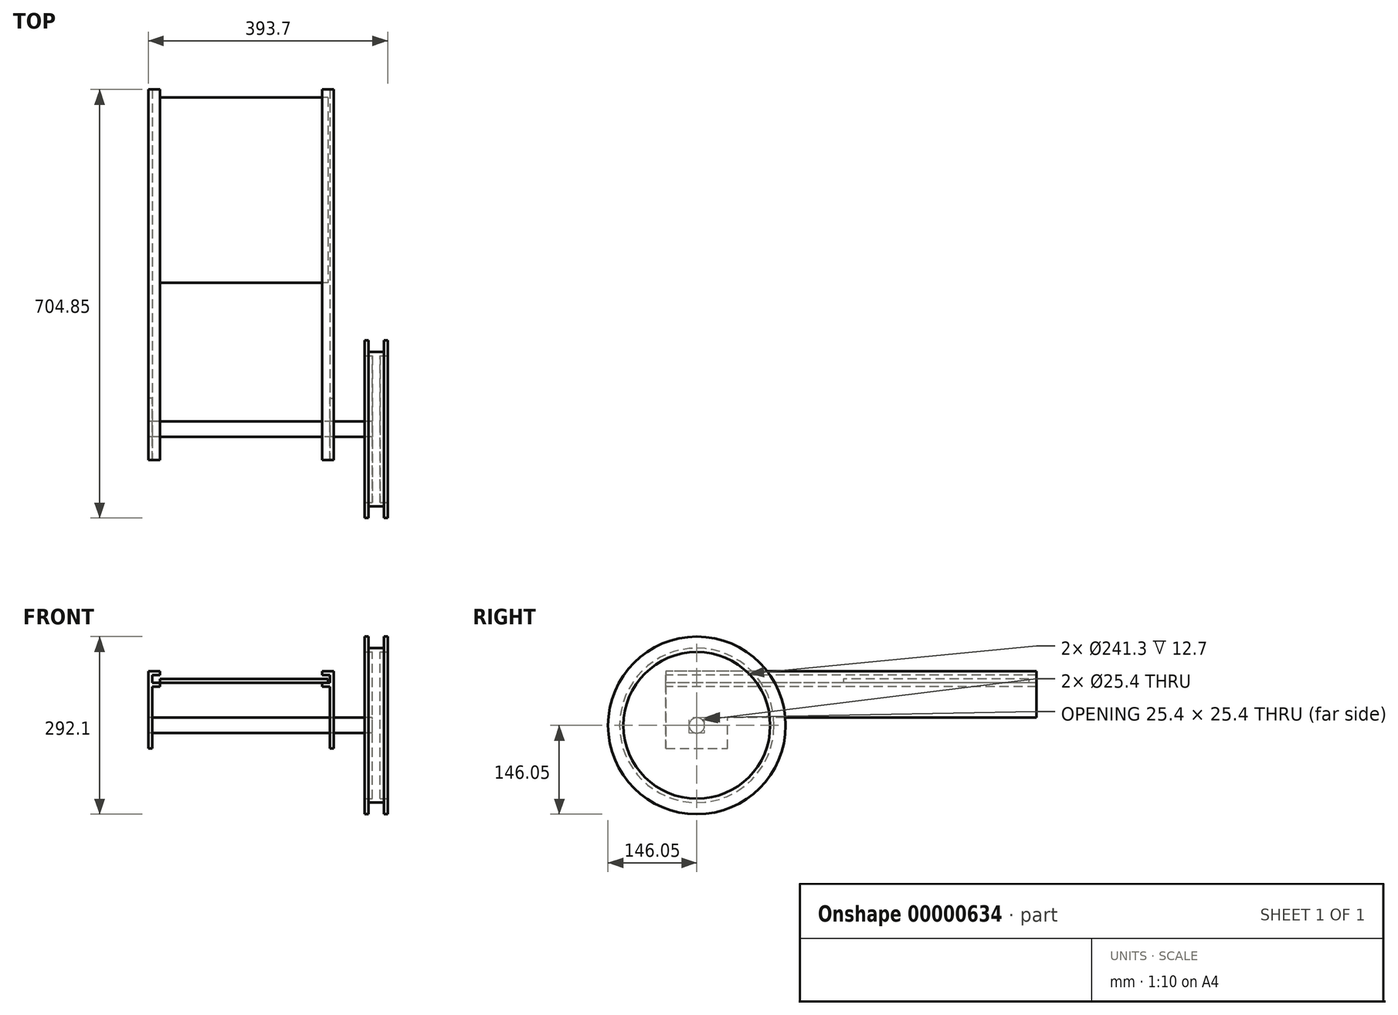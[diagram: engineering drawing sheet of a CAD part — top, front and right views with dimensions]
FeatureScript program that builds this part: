
annotation { "Feature Type Name" : "Feature", "Feature Type Description" : "" }
export const myFeature = defineFeature(function(context is Context, id is Id, definition is map)
    precondition{}
    {
        {
            var Q0;
            Q0=qCreatedBy(makeId("Front.planeOp"),FACE);
            var sketch = newSketch(context, id + "F0", { "sketchPlane" : qUnion([Q0])});
            skLineSegment(sketch, "E0", {"start": v(-152.4, 76.2) * mm, "end": v(-152.4, -50.8) * mm});
            skLineSegment(sketch, "E1", {"start": v(-152.4, -50.8) * mm, "end": v(-146.05, -50.8) * mm});
            skLineSegment(sketch, "E2", {"start": v(-146.05, 50.8) * mm, "end": v(-133.35, 50.8) * mm});
            skLineSegment(sketch, "E3", {"start": v(-133.35, 57.15) * mm, "end": v(-146.05, 57.15) * mm});
            skLineSegment(sketch, "E4", {"start": v(-146.05, 57.15) * mm, "end": v(-146.05, 69.85) * mm});
            skLineSegment(sketch, "E5", {"start": v(-146.05, 69.85) * mm, "end": v(-133.35, 69.85) * mm});
            skLineSegment(sketch, "E6", {"start": v(-133.35, 50.8) * mm, "end": v(-133.35, 57.15) * mm});
            skLineSegment(sketch, "E7", {"start": v(-133.35, 76.2) * mm, "end": v(-152.4, 76.2) * mm});
            skLineSegment(sketch, "E8", {"start": v(-146.05, -50.8) * mm, "end": v(-146.05, 50.8) * mm});
            skLineSegment(sketch, "E9", {"start": v(-146.05, 0) * mm, "end": v(-152.4, 0) * mm});
            skLineSegment(sketch, "E10", {"start": v(-133.35, 76.2) * mm, "end": v(-133.35, 69.85) * mm});
            skLineSegment(sketch, "E11", {"start": v(0, 0) * mm, "end": v(0, 73.55) * mm, "construction": true});
            skLineSegment(sketch, "E12.0.MirrorCS", {"start": v(146.05, -50.8) * mm, "end": v(146.05, 50.8) * mm});
            skLineSegment(sketch, "E12.1.MirrorCS", {"start": v(133.35, 50.8) * mm, "end": v(133.35, 57.15) * mm});
            skLineSegment(sketch, "E12.2.MirrorCS", {"start": v(146.05, 50.8) * mm, "end": v(133.35, 50.8) * mm});
            skLineSegment(sketch, "E12.3.MirrorCS", {"start": v(133.35, 76.2) * mm, "end": v(152.4, 76.2) * mm});
            skLineSegment(sketch, "E12.4.MirrorCS", {"start": v(152.4, -50.8) * mm, "end": v(146.05, -50.8) * mm});
            skLineSegment(sketch, "E12.5.MirrorCS", {"start": v(146.05, 69.85) * mm, "end": v(133.35, 69.85) * mm});
            skLineSegment(sketch, "E12.6.MirrorCS", {"start": v(146.05, 0) * mm, "end": v(152.4, 0) * mm});
            skLineSegment(sketch, "E12.7.MirrorCS", {"start": v(133.35, 57.15) * mm, "end": v(146.05, 57.15) * mm});
            skLineSegment(sketch, "E12.8.MirrorCS", {"start": v(133.35, 76.2) * mm, "end": v(133.35, 69.85) * mm});
            skLineSegment(sketch, "E12.9.MirrorCS", {"start": v(146.05, 57.15) * mm, "end": v(146.05, 69.85) * mm});
            skLineSegment(sketch, "E12.10.MirrorCS", {"start": v(152.4, 76.2) * mm, "end": v(152.4, -50.8) * mm});
            skSolve(sketch);
        }
        {
            var Q0;
            {var subQ2=sQuery(id+"F0.wireOp",EDGE,"E2");Q0=makeQuery(id+"F0.imprint","IMPRINT",FACE,{"disambiguationData":[TD([[makeQuery(id+"F0.imprint","IMPRINT",EDGE,{"derivedFrom":subQ2}),1.0]])]});}
            var Q1;
            Q1=makeQuery(id+"F0.imprint","IMPRINT",FACE,{"disambiguationData":[TD([[makeQuery(id+"F0.imprint","IMPRINT",EDGE,{"derivedFrom":sQuery(id+"F0.wireOp",EDGE,"E12.1.MirrorCS")}),-1.0]])]});
            extrude(context, id + "F1", {"entities" : qUnion([Q0, Q1]), "oppositeDirection" : true, "depth" : 508 * mm});
        }
        {
            var Q0;
            {var subQ2=sQuery(id+"F0.wireOp",EDGE,"E2");Q0=makeQuery(id+"F0.imprint","IMPRINT",FACE,{"disambiguationData":[TD([[makeQuery(id+"F0.imprint","IMPRINT",EDGE,{"derivedFrom":subQ2}),1.0]])]});}
            var Q1;
            {var subQ2=sQuery(id+"F0.wireOp",EDGE,"E1");Q1=makeQuery(id+"F0.imprint","IMPRINT",FACE,{"disambiguationData":[TD([[makeQuery(id+"F0.imprint","IMPRINT",EDGE,{"derivedFrom":subQ2}),1.0]])]});}
            var Q2;
            Q2=makeQuery(id+"F0.imprint","IMPRINT",FACE,{"disambiguationData":[TD([[makeQuery(id+"F0.imprint","IMPRINT",EDGE,{"derivedFrom":sQuery(id+"F0.wireOp",EDGE,"E12.1.MirrorCS")}),-1.0]])]});
            var Q3;
            {var subQ2=sQuery(id+"F0.wireOp",EDGE,"E12.4.MirrorCS");Q3=makeQuery(id+"F0.imprint","IMPRINT",FACE,{"disambiguationData":[TD([[makeQuery(id+"F0.imprint","IMPRINT",EDGE,{"derivedFrom":subQ2}),-1.0]])]});}
            extrude(context, id + "F2", {"entities" : qUnion([Q0, Q1, Q2, Q3]), "operationType" : NewBodyOperationType.ADD, "depth" : 101.6 * mm});
        }
        {
            var Q0;
            {var subQ0=sQuery(id+"F0.wireOp",EDGE,"E0");Q0=makeQuery(id+"F2.boolean.opBoolean","MERGE",FACE,{"derivedFrom":[makeQuery(id+"F1.opExtrude","SWEPT_FACE",FACE,{"disambiguationData":[OSD([subQ0])]}),makeQuery(id+"F2.opExtrude","SWEPT_FACE",FACE,{"disambiguationData":[OSD([subQ0])]})]});}
            var sketch = newSketch(context, id + "F3", { "sketchPlane" : qUnion([Q0])});
            skLineSegment(sketch, "E13.0", {"start": v(101.6, 76.2) * mm, "end": v(101.6, -50.8) * mm});
            skLineSegment(sketch, "E13.1", {"start": v(101.6, -50.8) * mm, "end": v(0, -50.8) * mm});
            skLineSegment(sketch, "E14.0", {"start": v(0, 76.2) * mm, "end": v(0, -50.8) * mm});
            skCircle(sketch, "E15", {"center": v(50.8, -12.7) * mm, "radius": 12.7 * mm});
            skLineSegment(sketch, "E16", {"start": v(50.8, -50.8) * mm, "end": v(50.8, 76.2) * mm, "construction": true});
            skSolve(sketch);
        }
        {
            var Q0;
            Q0=makeQuery(id+"F3.imprint","IMPRINT",FACE,{"disambiguationData":[TD([[makeQuery(id+"F3.imprint","IMPRINT",EDGE,{"derivedFrom":sQuery(id+"F3.wireOp",EDGE,"E15")}),1.0]])]});
            extrude(context, id + "F4", {"entities" : qUnion([Q0]), "operationType" : NewBodyOperationType.REMOVE, "endBound" : BoundingType.THROUGH_ALL, "oppositeDirection" : true, "depth" : 25.4 * mm});
        }
        {
            var Q0;
            Q0=makeQuery(id+"F3.imprint","IMPRINT",FACE,{"disambiguationData":[TD([[makeQuery(id+"F3.imprint","IMPRINT",EDGE,{"derivedFrom":sQuery(id+"F3.wireOp",EDGE,"E15")}),1.0]])]});
            extrude(context, id + "F5", {"entities" : qUnion([Q0]), "oppositeDirection" : true, "depth" : 381 * mm});
        }
        {
            var Q0;
            Q0=qCreatedBy(makeId("Top.planeOp"),FACE);
            var Q1;
            Q1=sQuery(id+"F3.wireOp",VERTEX,"E15.center");
            cPlane(context, id + "F6", {"entities" : qUnion([Q0, Q1]), "cplaneType" : CPlaneType.PLANE_POINT, "offset" : 152.4 * mm, "width" : 152.4 * mm, "height" : 152.4 * mm});
        }
        {
            var Q0;
            Q0=qCreatedBy(id+"F6.planeOp",FACE);
            var sketch = newSketch(context, id + "F7", { "sketchPlane" : qUnion([Q0])});
            skLineSegment(sketch, "E17.0", {"start": v(228.6, -63.5) * mm, "end": v(228.6, -38.1) * mm});
            skLineSegment(sketch, "E18", {"start": v(228.6, -38.1) * mm, "end": v(215.9, -38.1) * mm});
            skLineSegment(sketch, "E19", {"start": v(215.9, -38.1) * mm, "end": v(215.9, 69.85) * mm});
            skLineSegment(sketch, "E20", {"start": v(222.25, 76.2) * mm, "end": v(222.25, -38.1) * mm});
            skLineSegment(sketch, "E21", {"start": v(228.6, -50.8) * mm, "end": v(181.47, -50.8) * mm, "construction": true});
            skLineSegment(sketch, "E22", {"start": v(222.25, 76.2) * mm, "end": v(209.55, 76.2) * mm});
            skLineSegment(sketch, "E23", {"start": v(209.55, 76.2) * mm, "end": v(209.55, 95.25) * mm});
            skLineSegment(sketch, "E24", {"start": v(209.55, 95.25) * mm, "end": v(203.2, 95.25) * mm});
            skLineSegment(sketch, "E25", {"start": v(203.2, 95.25) * mm, "end": v(203.2, 69.85) * mm});
            skLineSegment(sketch, "E26", {"start": v(203.2, 69.85) * mm, "end": v(215.9, 69.85) * mm});
            skLineSegment(sketch, "E27.0.MirrorCS", {"start": v(228.6, -38.1) * mm, "end": v(228.6, 69.85) * mm});
            skLineSegment(sketch, "E28.0.MirrorCS", {"start": v(222.25, 76.2) * mm, "end": v(234.95, 76.2) * mm});
            skLineSegment(sketch, "E29.0.MirrorCS", {"start": v(234.95, 76.2) * mm, "end": v(234.95, 95.25) * mm});
            skLineSegment(sketch, "E30.0.MirrorCS", {"start": v(241.3, 95.25) * mm, "end": v(241.3, 69.85) * mm});
            skLineSegment(sketch, "E31.0.MirrorCS", {"start": v(241.3, 69.85) * mm, "end": v(228.6, 69.85) * mm});
            skLineSegment(sketch, "E32.0.MirrorCS", {"start": v(234.95, 95.25) * mm, "end": v(241.3, 95.25) * mm});
            skSolve(sketch);
        }
        {
            var Q0;
            {var subQ1=sQuery(id+"F7.wireOp",EDGE,"E20");Q0=makeQuery(id+"F7.imprint","IMPRINT",FACE,{"disambiguationData":[TD([[makeQuery(id+"F7.imprint","IMPRINT",EDGE,{"derivedFrom":subQ1}),1.0]])]});}
            var Q1;
            {var subQ1=sQuery(id+"F7.wireOp",EDGE,"E19");Q1=makeQuery(id+"F7.imprint","IMPRINT",FACE,{"disambiguationData":[TD([[makeQuery(id+"F7.imprint","IMPRINT",EDGE,{"derivedFrom":subQ1}),-1.0]])]});}
            var Q2;
            Q2=sQuery(id+"F7.wireOp",EDGE,"E21");
            revolve(context, id + "F8", {"operationType" : NewBodyOperationType.ADD, "entities" : qUnion([Q0, Q1]), "axis" : qUnion([Q2]), "revolveType" : RevolveType.FULL});
        }
        {
            var Q0;
            {var subQ0=sQuery(id+"F0.wireOp",EDGE,"E3");Q0=makeQuery(id+"F2.boolean.opBoolean","MERGE",FACE,{"derivedFrom":[makeQuery(id+"F1.opExtrude","SWEPT_FACE",FACE,{"disambiguationData":[OSD([subQ0])]}),makeQuery(id+"F2.opExtrude","SWEPT_FACE",FACE,{"disambiguationData":[OSD([subQ0])]})]});}
            var sketch = newSketch(context, id + "F9", { "sketchPlane" : qUnion([Q0])});
            skLineSegment(sketch, "E33.0", {"start": v(142.88, 494.81) * mm, "end": v(142.88, -101.6) * mm});
            skLineSegment(sketch, "E34.0", {"start": v(-142.88, 494.81) * mm, "end": v(-142.88, -101.6) * mm});
            skLineSegment(sketch, "E35", {"start": v(142.88, 494.81) * mm, "end": v(-142.88, 494.81) * mm});
            skLineSegment(sketch, "E36", {"start": v(142.88, 190.01) * mm, "end": v(-142.88, 190.01) * mm});
            skSolve(sketch);
        }
        {
            var Q0;
            {var subQ5=sQuery(id+"F9.wireOp",EDGE,"E35");var subQ7=sQuery(id+"F9.wireOp",EDGE,"E33.0");var subQ9=makeQuery(id+"F9.imprint","INTERSECT",VERTEX,{"derivedFrom":[subQ7,subQ5]});Q0=makeQuery(id+"F9.imprint","IMPRINT",FACE,{"disambiguationData":[TD([[makeQuery(id+"F9.imprint","IMPRINT",EDGE,{"disambiguationData":[TD([[subQ9,-1.0]])],"derivedFrom":subQ7}),-1.0]])]});}
            extrude(context, id + "F10", {"entities" : qUnion([Q0]), "operationType" : NewBodyOperationType.ADD, "depth" : 6.35 * mm});
        }
    });
